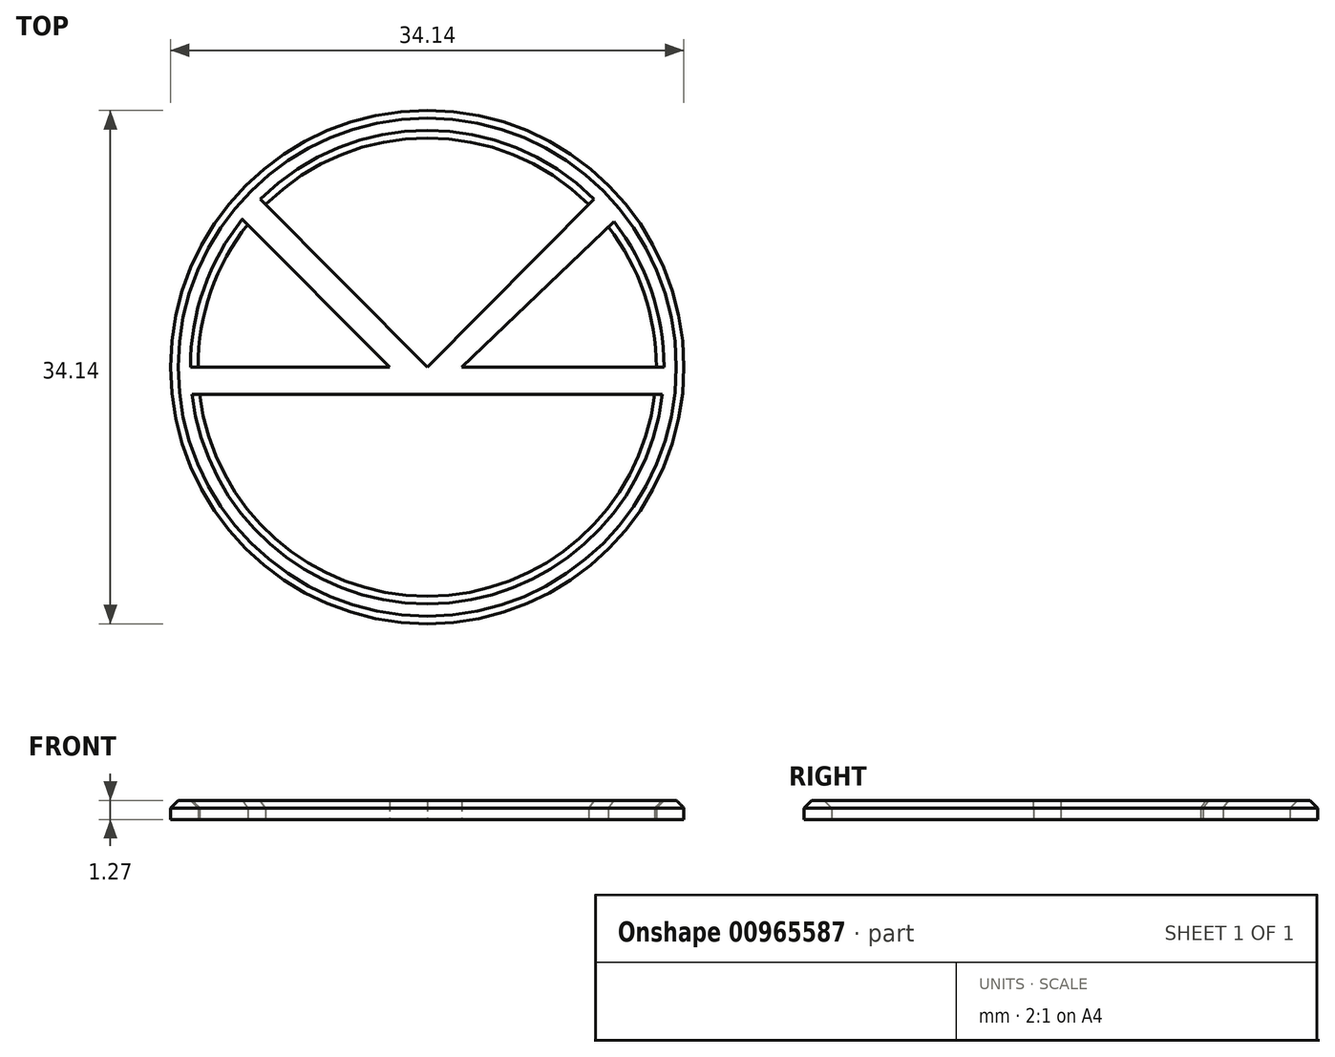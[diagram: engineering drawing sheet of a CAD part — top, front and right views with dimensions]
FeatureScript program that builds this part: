
annotation { "Feature Type Name" : "Feature", "Feature Type Description" : "" }
export const myFeature = defineFeature(function(context is Context, id is Id, definition is map)
    precondition{}
    {
        {
            var Q0;
            Q0=qCreatedBy(makeId("Top.planeOp"),FACE);
            var sketch = newSketch(context, id + "F0", { "sketchPlane" : qUnion([Q0])});
            skCircle(sketch, "E0", {"center": v(0, 0) * mm, "radius": 15.24 * mm});
            skLineSegment(sketch, "E1", {"start": v(-15.13, -1.82) * mm, "end": v(15.13, -1.82) * mm});
            skLineSegment(sketch, "E2", {"start": v(-15.24, 0) * mm, "end": v(15.24, 0) * mm});
            skLineSegment(sketch, "E3", {"start": v(0, 0) * mm, "end": v(10.74, 10.8) * mm});
            skLineSegment(sketch, "E4", {"start": v(2.3, 0) * mm, "end": v(12.06, 9.32) * mm});
            skCircle(sketch, "E5", {"center": v(0, 0) * mm, "radius": 17.07 * mm});
            skLineSegment(sketch, "E6", {"start": v(-10.74, 10.8) * mm, "end": v(0, 0) * mm});
            skLineSegment(sketch, "E7", {"start": v(-9.55, 7.08) * mm, "end": v(-2.5, 0) * mm});
            skLineSegment(sketch, "E8", {"start": v(-2.5, 0) * mm, "end": v(-11.93, 9.48) * mm});
            skSolve(sketch);
        }
        {
            var Q0;
            Q0=makeQuery(id+"F0.imprint","IMPRINT",FACE,{"disambiguationData":[TD([[makeQuery(id+"F0.imprint","IMPRINT",EDGE,{"derivedFrom":sQuery(id+"F0.wireOp",EDGE,"E5")}),1.0]])]});
            var Q1;
            {var subQ1=sQuery(id+"F0.wireOp",EDGE,"E6");Q1=makeQuery(id+"F0.imprint","IMPRINT",FACE,{"disambiguationData":[TD([[makeQuery(id+"F0.imprint","IMPRINT",EDGE,{"derivedFrom":subQ1}),-1.0]])]});}
            var Q2;
            {var subQ0=sQuery(id+"F0.wireOp",EDGE,"E3");Q2=makeQuery(id+"F0.imprint","IMPRINT",FACE,{"disambiguationData":[TD([[makeQuery(id+"F0.imprint","IMPRINT",EDGE,{"derivedFrom":subQ0}),-1.0]])]});}
            var Q3;
            {var subQ4=sQuery(id+"F0.wireOp",EDGE,"E1");Q3=makeQuery(id+"F0.imprint","IMPRINT",FACE,{"disambiguationData":[TD([[makeQuery(id+"F0.imprint","IMPRINT",EDGE,{"derivedFrom":subQ4}),1.0]])]});}
            extrude(context, id + "F1", {"entities" : qUnion([Q0, Q1, Q2, Q3]), "depth" : 1.27 * mm, "offsetDistance" : 25.4 * mm});
        }
        {
            var Q0;
            Q0=makeQuery(id+"F1.opExtrude","CAP_EDGE",EDGE,{"disambiguationData":[OSD([sQuery(id+"F0.wireOp",EDGE,"E5")])],"isStart":false});
            var Q1;
            {var subQ0=sQuery(id+"F0.wireOp",EDGE,"E1");var subQ1=sQuery(id+"F0.wireOp",EDGE,"E0");Q1=makeQuery(id+"F1.opExtrude","CAP_EDGE",EDGE,{"disambiguationData":[OSD([subQ1]),TDD([makeQuery(id+"F0.imprint","IMPRINT",EDGE,{"disambiguationData":[TD([[makeQuery(id+"F0.imprint","INTERSECT",VERTEX,{"disambiguationData":[OD(0.0)],"derivedFrom":[subQ1,subQ0]}),-1.0]])],"derivedFrom":subQ1})])],"isStart":false});}
            var Q2;
            {var subQ0=sQuery(id+"F0.wireOp",EDGE,"E0");Q2=makeQuery(id+"F1.opExtrude","CAP_EDGE",EDGE,{"disambiguationData":[OSD([subQ0]),TDD([makeQuery(id+"F0.imprint","IMPRINT",EDGE,{"disambiguationData":[TD([[makeQuery(id+"F0.imprint","INTERSECT",VERTEX,{"derivedFrom":[subQ0,sQuery(id+"F0.wireOp",EDGE,"E8")]}),-1.0]])],"derivedFrom":subQ0})])],"isStart":false});}
            var Q3;
            {var subQ0=sQuery(id+"F0.wireOp",EDGE,"E0");Q3=makeQuery(id+"F1.opExtrude","CAP_EDGE",EDGE,{"disambiguationData":[OSD([subQ0]),TDD([makeQuery(id+"F0.imprint","IMPRINT",EDGE,{"disambiguationData":[TD([[makeQuery(id+"F0.imprint","INTERSECT",VERTEX,{"derivedFrom":[subQ0,sQuery(id+"F0.wireOp",EDGE,"E3")]}),-1.0]])],"derivedFrom":subQ0})])],"isStart":false});}
            var Q4;
            {var subQ0=sQuery(id+"F0.wireOp",EDGE,"E0");Q4=makeQuery(id+"F1.opExtrude","CAP_EDGE",EDGE,{"disambiguationData":[OSD([subQ0]),TDD([makeQuery(id+"F0.imprint","IMPRINT",EDGE,{"disambiguationData":[TD([[makeQuery(id+"F0.imprint","INTERSECT",VERTEX,{"derivedFrom":[subQ0,sQuery(id+"F0.wireOp",EDGE,"E4")]}),1.0]])],"derivedFrom":subQ0})])],"isStart":false});}
            chamfer(context, id + "F2", {"entities" : qUnion([Q0, Q1, Q2, Q3, Q4]), "width" : 0.5 * mm, "tangentPropagation" : true});
        }
    });
